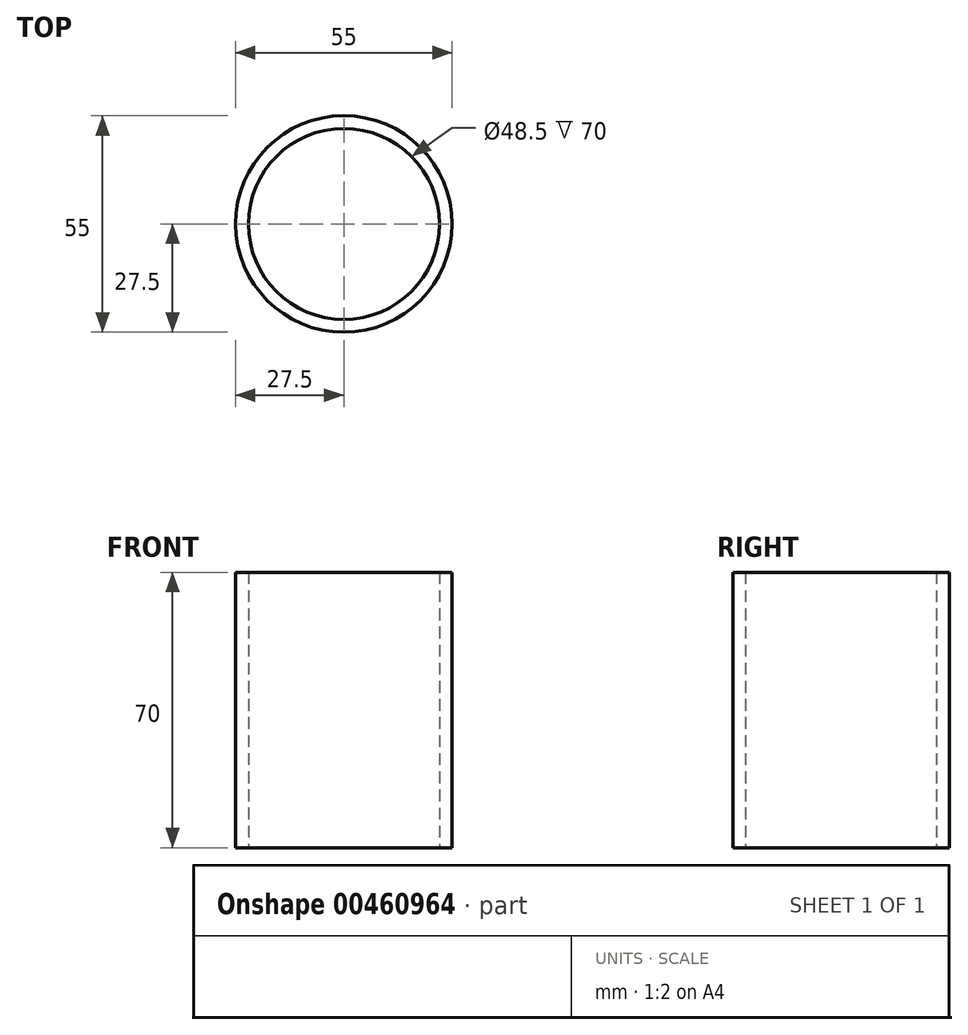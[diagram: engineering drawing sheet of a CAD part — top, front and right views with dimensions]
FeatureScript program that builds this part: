
annotation { "Feature Type Name" : "Feature", "Feature Type Description" : "" }
export const myFeature = defineFeature(function(context is Context, id is Id, definition is map)
    precondition{}
    {
        {
            var Q0;
            Q0=qCreatedBy(makeId("Top.planeOp"),FACE);
            var sketch = newSketch(context, id + "F0", { "sketchPlane" : qUnion([Q0])});
            skCircle(sketch, "E0", {"center": v(0, 0) * mm, "radius": 24.25 * mm});
            skCircle(sketch, "E1", {"center": v(0, 0) * mm, "radius": 27.5 * mm});
            skSolve(sketch);
        }
        {
            var Q0;
            Q0=makeQuery(id+"F0.imprint","IMPRINT",FACE,{"disambiguationData":[TD([[makeQuery(id+"F0.imprint","IMPRINT",EDGE,{"derivedFrom":sQuery(id+"F0.wireOp",EDGE,"E0")}),-1.0]])]});
            extrude(context, id + "F1", {"entities" : qUnion([Q0]), "depth" : 70 * mm});
        }
    });
